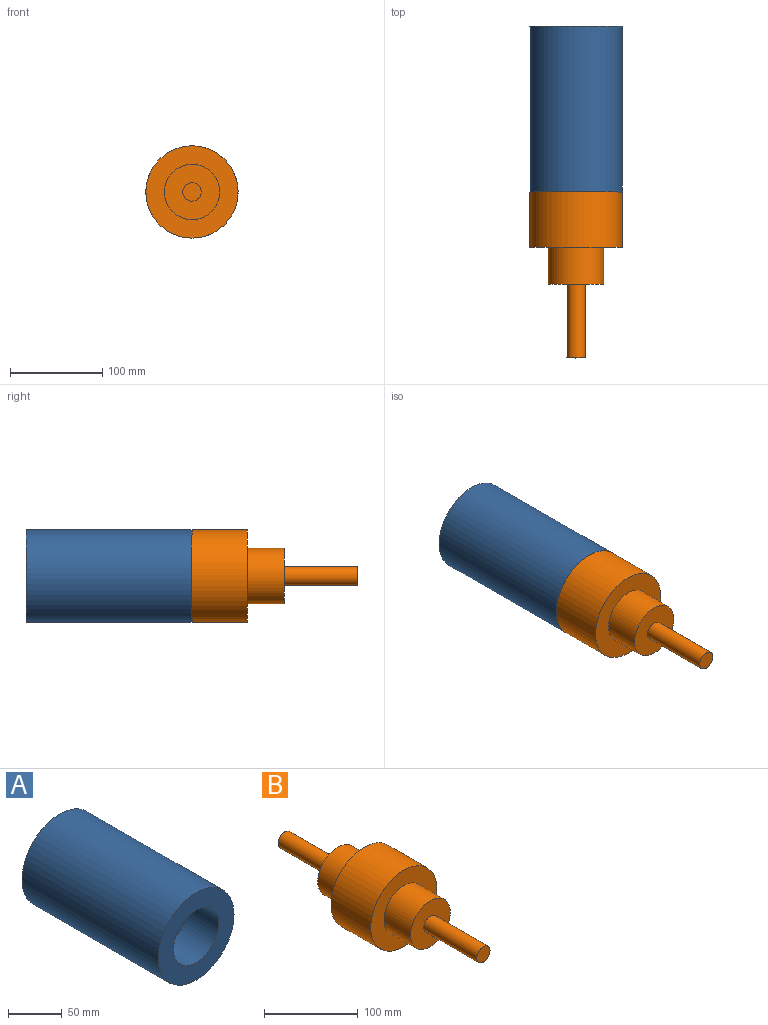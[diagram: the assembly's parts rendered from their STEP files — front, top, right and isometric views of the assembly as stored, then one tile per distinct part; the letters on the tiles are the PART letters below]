
ASSEMBLY  parts=2 mates=1
PART A: 7 faces, bbox 100x180x100 mm
  f0: cylinder r=50mm len=180mm, axis (0,1,0), area 56548.7mm2, adj f1,f3
  f1: plane 100x100mm, normal (0,1,0), area 7854mm2, adj f0
  f2: cylinder r=30mm len=60mm, axis (0,1,0), area 7539.8mm2, adj f3,f4
  f3: plane 100x100mm, normal (0,-1,0), area 5026.5mm2, adj f0,f2
  f4: plane 60x60mm, normal (0,-1,0), area 2513.3mm2, adj f2,f5
  f5: cylinder r=10mm len=80mm, axis (0,-1,0), area 5026.5mm2, adj f4,f6
  f6: plane 20x20mm, normal (0,-1,0), area 314.2mm2, adj f5
PART B: 11 faces, bbox 100x300x100 mm
  f0: cylinder r=50mm len=100mm, axis (0,1,0), area 18849.6mm2, adj f1,f2
  f1: plane 100x100mm, normal (0,-1,0), area 5026.5mm2, adj f0,f5
  f2: plane 100x100mm, normal (0,1,0), area 5026.5mm2, adj f0,f3
  f3: cylinder r=30mm len=60mm, axis (0,-1,0), area 7539.8mm2, adj f2,f4
  f4: plane 60x60mm, normal (0,1,0), area 2513.3mm2, adj f3,f9
  f5: cylinder r=30mm len=60mm, axis (0,1,0), area 7539.8mm2, adj f1,f6
  f6: plane 60x60mm, normal (0,-1,0), area 2513.3mm2, adj f5,f7
  f7: cylinder r=10mm len=80mm, axis (0,1,0), area 5026.5mm2, adj f6,f8
  f8: plane 20x20mm, normal (0,-1,0), area 314.2mm2, adj f7
  f9: cylinder r=10mm len=80mm, axis (0,-1,0), area 5026.5mm2, adj f4,f10
  f10: plane 20x20mm, normal (0,1,0), area 314.2mm2, adj f9
PLACE A t=(-146.09,79.83,-11.54)mm
PLACE B t=(-146.09,-130.17,-11.54)mm
MATE fastened A.f0 <-> B.f0  axis (0,-1,0) through (-146.09,-100.17,-11.54)mm
